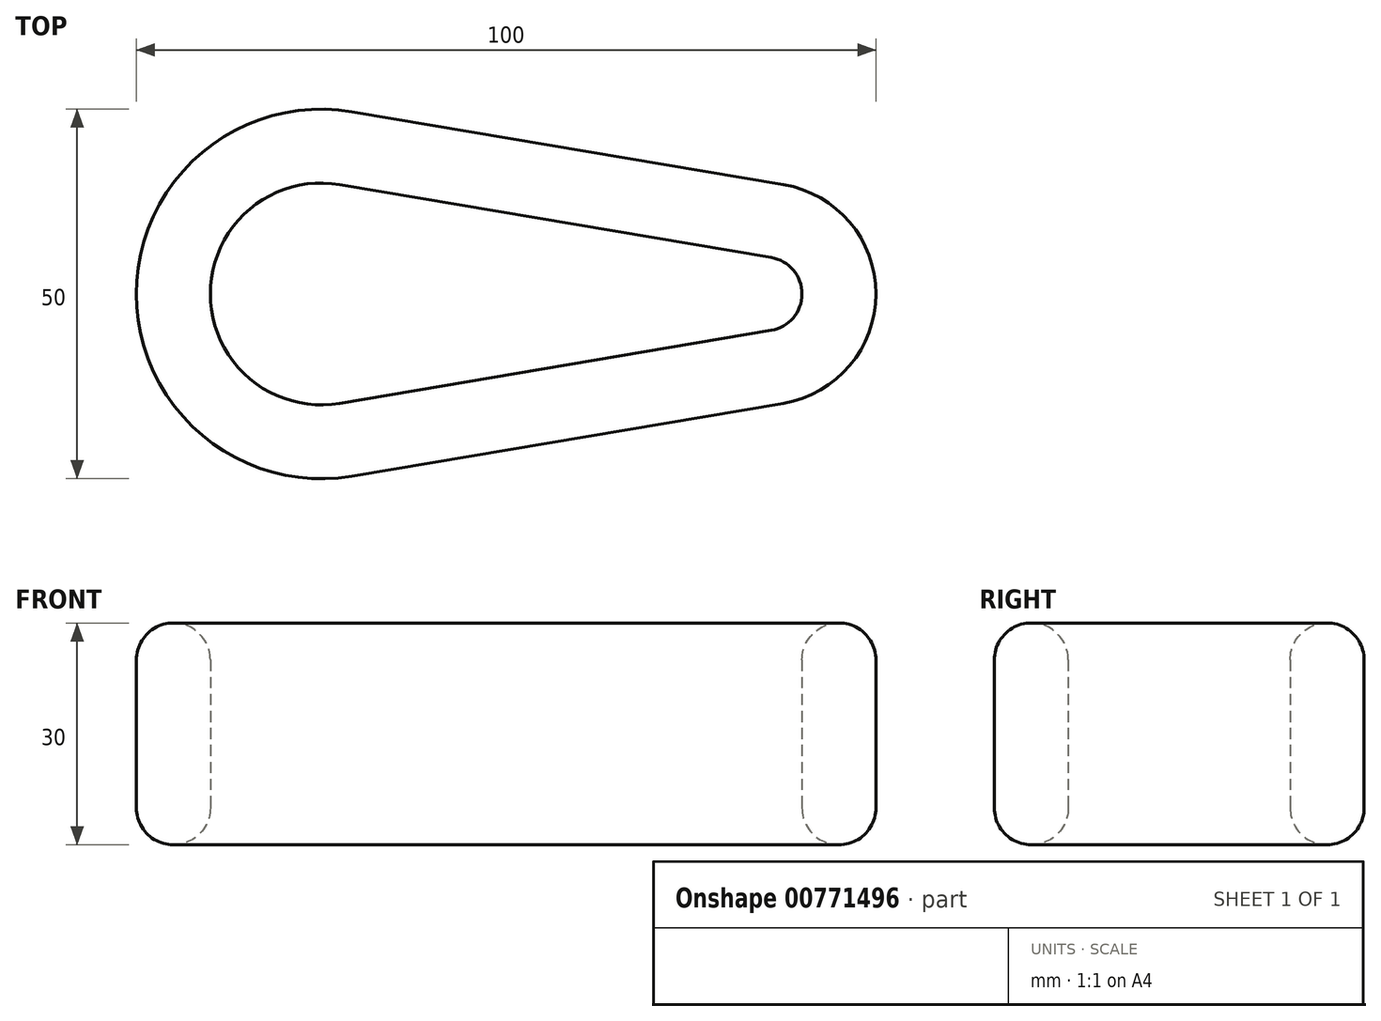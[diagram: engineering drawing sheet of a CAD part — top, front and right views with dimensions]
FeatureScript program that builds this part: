
annotation { "Feature Type Name" : "Feature", "Feature Type Description" : "" }
export const myFeature = defineFeature(function(context is Context, id is Id, definition is map)
    precondition{}
    {
        {
            var Q0;
            Q0=qCreatedBy(makeId("Top.planeOp"),FACE);
            var sketch = newSketch(context, id + "F0", { "sketchPlane" : qUnion([Q0])});
            skArc(sketch, "E0", {"start": v(4.17, 24.65) * mm, "mid": v(-25, 0) * mm, "end": v(4.17, -24.65) * mm});
            skArc(sketch, "E1", {"start": v(62.5, -14.8) * mm, "mid": v(75, 0) * mm, "end": v(62.5, 14.8) * mm});
            skLineSegment(sketch, "E2", {"start": v(4.17, 24.65) * mm, "end": v(62.5, 14.8) * mm});
            skLineSegment(sketch, "E3", {"start": v(0, 0) * mm, "end": v(67.53, 0) * mm, "construction": true});
            skLineSegment(sketch, "E4.MirrorCS", {"start": v(4.17, -24.65) * mm, "end": v(62.5, -14.8) * mm});
            skLineSegment(sketch, "E5.0", {"start": v(2.5, -14.8) * mm, "end": v(60.83, -4.93) * mm});
            skLineSegment(sketch, "E6.0", {"start": v(2.5, 14.8) * mm, "end": v(60.83, 4.93) * mm});
            skArc(sketch, "E7.0", {"start": v(2.5, 14.8) * mm, "mid": v(-15, 0) * mm, "end": v(2.5, -14.8) * mm});
            skArc(sketch, "E8.0", {"start": v(60.83, -4.93) * mm, "mid": v(65, 0) * mm, "end": v(60.83, 4.93) * mm});
            skSolve(sketch);
        }
        {
            var Q0;
            Q0 = qSketchRegion(id + "F0", true);
            extrude(context, id + "F1", {"entities" : qUnion([Q0]), "depth" : 30 * mm, "offsetDistance" : 25.4 * mm});
        }
        {
            var Q0;
            Q0=makeQuery(id+"F1.opExtrude","CAP_FACE",FACE,{"disambiguationData":[OSD([sQuery(id+"F0.wireOp",EDGE,"E0"),sQuery(id+"F0.wireOp",EDGE,"E1"),sQuery(id+"F0.wireOp",EDGE,"E2"),sQuery(id+"F0.wireOp",EDGE,"E4.MirrorCS"),sQuery(id+"F0.wireOp",EDGE,"E5.0"),sQuery(id+"F0.wireOp",EDGE,"E6.0"),sQuery(id+"F0.wireOp",EDGE,"E7.0"),sQuery(id+"F0.wireOp",EDGE,"E8.0")])],"isStart":false});
            var Q1;
            Q1=makeQuery(id+"F1.opExtrude","CAP_FACE",FACE,{"disambiguationData":[OSD([sQuery(id+"F0.wireOp",EDGE,"E0"),sQuery(id+"F0.wireOp",EDGE,"E1"),sQuery(id+"F0.wireOp",EDGE,"E2"),sQuery(id+"F0.wireOp",EDGE,"E4.MirrorCS"),sQuery(id+"F0.wireOp",EDGE,"E5.0"),sQuery(id+"F0.wireOp",EDGE,"E6.0"),sQuery(id+"F0.wireOp",EDGE,"E7.0"),sQuery(id+"F0.wireOp",EDGE,"E8.0")])],"isStart":true});
            fillet(context, id + "F2", {"entities" : qUnion([Q0, Q1]), "radius" : 5 * mm, "tangentPropagation" : true, "allowEdgeOverflow" : false});
        }
    });
